# Revit family: LOMD-01-LE
name_source: partatom
category: Lighting Fixtures
revit_build: Autodesk Revit 2014 (Build: 20130308_1515(x64)
units: mm (PartAtom-declared; Revit-internal decimal feet)

## types (2) — shared parameters
Assembly Code = D5020200
Certification = EU Type Examination Certificate
 CML16ATEX1020X
IECEx Certificate of Conformity
 IECEx CML16.0016X
Color Filter = 16777215
Connector Description = Lighting Connector
Default Elevation = 1219.2 mm  [stored 4 ft]
Description = The Lomond is a rugged, flameproof LED luminaire. It features
an integrated mounting channel for universal installation. The
aluminium and glass construction make the Lomond highly
resistant to aggressive chemical agents.
Dimming Lamp Color Temperature Shift = <None>
Drum-Height = 609.6 mm  [stored 2 ft]
Emit Shape Visible in Rendering = No
Emit from Rectangle Length = 50 mm  [stored 0.164042 ft]
Emit from Rectangle Width = 720 mm  [stored 2.3622 ft]
Features = Suitable for high ambient areas.
Highly Energy Efficient.
Cool running improves T-rating.
IP68 version available
Fixture distribution = Direct
Housing Material = Paint - Hubbell - Matte White
IP Rating = IP66/67
Lamp = LED
Length = 927 mm  [stored 3.04134 ft]
Load Classification = Lighting
Manufacturer = Chalmit
Mounting = Paint - Hubbell - Light Silver
Power Factor = 1
Product Documentation Link = https://hubbellcdn.com
Product Link = https://www.hubbell.com
Reflector Finish = Hubbell - White Glass
Surge Protection = 4kV
Tilt Angle = 90.00°
Types of protection = Ex db (Flameproof)
Ex db eb (Flameproof, Increased Safety) [Emergency only]
Ex tb (Dust Protected Enclosure)
URL = https://www.hubbell.com
Voltage = 120 V
Warranty = 5 years Warranty
Width = 168.5 mm  [stored 0.552822 ft]
Wings = Paint - Hubbell - Light Silver

## per-type parameters (varying)
| type | Apparent Load | Model | Photometric Web File | Wattage Comments | Watts |
| LOMD/01L/LE | 20 VA | LMOD/01/LE | CHL_LOMD_01L_LE.ies | 20 W | 20 W |
| LOMD/01L/LE/EM | 24 VA | LOMD/01L/LE/EM | CHL_LOMD_01L_LE_EM.ies | 24W | 24 W |

note: [stored X ft] marks values corroborated as IEEE doubles in the binary element streams (Revit-internal decimal feet)

## geometry (parser evidence)
native form markers: Sweep x4
no freeform markers — native parametric forms only
